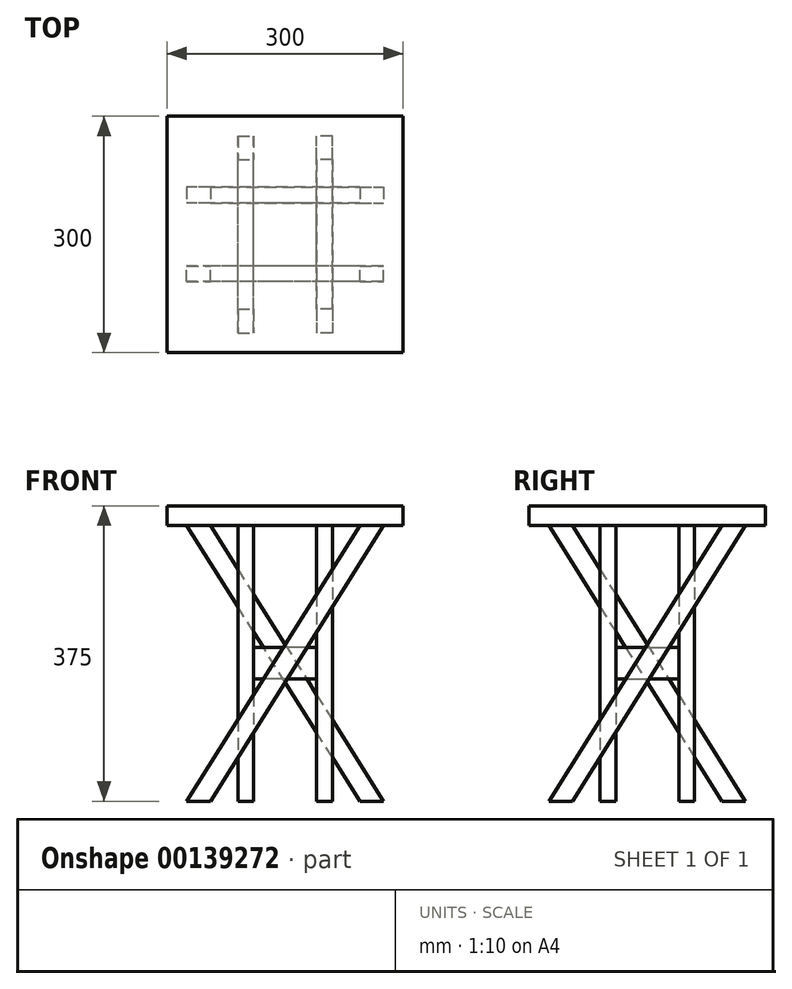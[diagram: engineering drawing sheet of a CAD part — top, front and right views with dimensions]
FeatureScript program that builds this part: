
annotation { "Feature Type Name" : "Feature", "Feature Type Description" : "" }
export const myFeature = defineFeature(function(context is Context, id is Id, definition is map)
    precondition{}
    {
        {
            var Q0;
            Q0=qCreatedBy(makeId("Top.planeOp"),FACE);
            var sketch = newSketch(context, id + "F0", { "sketchPlane" : qUnion([Q0])});
            skLineSegment(sketch, "E0.bottom", {"start": v(150, -150) * mm, "end": v(-150, -150) * mm});
            skLineSegment(sketch, "E0.top", {"start": v(150, 150) * mm, "end": v(-150, 150) * mm});
            skLineSegment(sketch, "E0.left", {"start": v(150, -150) * mm, "end": v(150, 150) * mm});
            skLineSegment(sketch, "E0.right", {"start": v(-150, -150) * mm, "end": v(-150, 150) * mm});
            skPoint(sketch, "E0.middle", {"position": v(0, 0) * mm});
            skLineSegment(sketch, "E1.bottom", {"start": v(40, -40) * mm, "end": v(-40, -40) * mm});
            skLineSegment(sketch, "E1.top", {"start": v(40, 40) * mm, "end": v(-40, 40) * mm});
            skLineSegment(sketch, "E1.left", {"start": v(40, -40) * mm, "end": v(40, 40) * mm});
            skLineSegment(sketch, "E1.right", {"start": v(-40, -40) * mm, "end": v(-40, 40) * mm});
            skSolve(sketch);
        }
        {
            var Q0;
            Q0=qCreatedBy(makeId("Front.planeOp"),FACE);
            var sketch = newSketch(context, id + "F1", { "sketchPlane" : qUnion([Q0])});
            skLineSegment(sketch, "E2.bottom", {"start": v(-125, 0) * mm, "end": v(125, 0) * mm, "construction": true});
            skLineSegment(sketch, "E2.top", {"start": v(-125, -350) * mm, "end": v(125, -350) * mm, "construction": true});
            skLineSegment(sketch, "E2.left", {"start": v(-125, 0) * mm, "end": v(-125, -350) * mm, "construction": true});
            skLineSegment(sketch, "E2.right", {"start": v(125, 0) * mm, "end": v(125, -350) * mm, "construction": true});
            skLineSegment(sketch, "E3", {"start": v(0, 0) * mm, "end": v(0, -350) * mm, "construction": true});
            skLineSegment(sketch, "E4", {"start": v(125, 0) * mm, "end": v(-125, -350) * mm, "construction": true});
            skLineSegment(sketch, "E5", {"start": v(-125, 0) * mm, "end": v(125, -350) * mm, "construction": true});
            skLineSegment(sketch, "E6", {"start": v(-95, 0) * mm, "end": v(125, -350) * mm});
            skLineSegment(sketch, "E7", {"start": v(95, -350) * mm, "end": v(-125, 0) * mm});
            skLineSegment(sketch, "E8", {"start": v(95, 0) * mm, "end": v(-125, -350) * mm});
            skLineSegment(sketch, "E9", {"start": v(125, 0) * mm, "end": v(-95, -350) * mm});
            skLineSegment(sketch, "E10", {"start": v(-125, -350) * mm, "end": v(-95, -350) * mm});
            skLineSegment(sketch, "E11", {"start": v(95, -350) * mm, "end": v(125, -350) * mm});
            skLineSegment(sketch, "E12", {"start": v(95, 0) * mm, "end": v(125, 0) * mm});
            skLineSegment(sketch, "E13", {"start": v(-95, 0) * mm, "end": v(-125, 0) * mm});
            skLineSegment(sketch, "E14", {"start": v(0, -175) * mm, "end": v(36.92, -175) * mm, "construction": true});
            skPoint(sketch, "E14.endSnap0", {"position": v(0, -175) * mm});
            skSolve(sketch);
        }
        {
            var Q0;
            Q0=makeQuery(id+"F0.imprint","IMPRINT",FACE,{"disambiguationData":[TD([[makeQuery(id+"F0.imprint","IMPRINT",EDGE,{"derivedFrom":sQuery(id+"F0.wireOp",EDGE,"E0.bottom")}),-1.0]])]});
            var Q1;
            Q1=sQuery(id+"F1.wireOp",EDGE,"E14");
            cPlane(context, id + "F2", {"entities" : qUnion([Q0, Q1]), "cplaneType" : CPlaneType.LINE_ANGLE, "offset" : 25 * mm, "angle" : 0 * degree, "width" : 150 * mm, "height" : 150 * mm});
        }
        {
            var Q0;
            Q0=qCreatedBy(id+"F2.planeOp",FACE);
            var sketch = newSketch(context, id + "F3", { "sketchPlane" : qUnion([Q0])});
            skLineSegment(sketch, "E15.0", {"start": v(-40, 40) * mm, "end": v(-40, -40) * mm});
            skLineSegment(sketch, "E15.1", {"start": v(40, -40) * mm, "end": v(-40, -40) * mm});
            skLineSegment(sketch, "E15.2", {"start": v(40, 40) * mm, "end": v(-40, 40) * mm});
            skLineSegment(sketch, "E15.3", {"start": v(40, 40) * mm, "end": v(40, -40) * mm});
            skSolve(sketch);
        }
        {
            var Q0;
            Q0=qCreatedBy(makeId("Front.planeOp"),FACE);
            var Q1;
            Q1=sQuery(id+"F3.wireOp",EDGE,"E15.1");
            cPlane(context, id + "F4", {"entities" : qUnion([Q0, Q1]), "cplaneType" : CPlaneType.LINE_ANGLE, "offset" : 25 * mm, "angle" : 0 * degree, "width" : 150 * mm, "height" : 150 * mm});
        }
        {
            var Q0;
            Q0=qCreatedBy(makeId("Front.planeOp"),FACE);
            var Q1;
            Q1=sQuery(id+"F3.wireOp",EDGE,"E15.2");
            cPlane(context, id + "F5", {"entities" : qUnion([Q0, Q1]), "cplaneType" : CPlaneType.LINE_ANGLE, "offset" : 25 * mm, "angle" : 0 * degree, "width" : 150 * mm, "height" : 150 * mm});
        }
        {
            var Q0;
            Q0=qCreatedBy(id+"F4.planeOp",FACE);
            var sketch = newSketch(context, id + "F6", { "sketchPlane" : qUnion([Q0])});
            skLineSegment(sketch, "E16.0", {"start": v(-95, -350) * mm, "end": v(125, 0) * mm});
            skLineSegment(sketch, "E16.1", {"start": v(95, 0) * mm, "end": v(-125, -350) * mm});
            skLineSegment(sketch, "E16.2", {"start": v(95, 0) * mm, "end": v(125, 0) * mm});
            skLineSegment(sketch, "E16.3", {"start": v(-95, -350) * mm, "end": v(-125, -350) * mm});
            skSolve(sketch);
        }
        {
            var Q0;
            Q0=qCreatedBy(id+"F5.planeOp",FACE);
            var sketch = newSketch(context, id + "F7", { "sketchPlane" : qUnion([Q0])});
            skLineSegment(sketch, "E17.0", {"start": v(-95, 0) * mm, "end": v(-125, 0) * mm});
            skLineSegment(sketch, "E17.1", {"start": v(-125, 0) * mm, "end": v(95, -350) * mm});
            skLineSegment(sketch, "E17.2", {"start": v(-95, 0) * mm, "end": v(125, -350) * mm});
            skLineSegment(sketch, "E17.3", {"start": v(125, -350) * mm, "end": v(95, -350) * mm});
            skSolve(sketch);
        }
        {
            var Q0;
            Q0=makeQuery(id+"F7.imprint","IMPRINT",FACE,{"disambiguationData":[TD([[makeQuery(id+"F7.imprint","IMPRINT",EDGE,{"derivedFrom":sQuery(id+"F7.wireOp",EDGE,"E17.0")}),1.0]])]});
            extrude(context, id + "F8", {"entities" : qUnion([Q0]), "oppositeDirection" : true, "depth" : 20 * mm});
        }
        {
            var Q0;
            Q0=makeQuery(id+"F6.imprint","IMPRINT",FACE,{"disambiguationData":[TD([[makeQuery(id+"F6.imprint","IMPRINT",EDGE,{"derivedFrom":sQuery(id+"F6.wireOp",EDGE,"E16.0")}),1.0]])]});
            extrude(context, id + "F9", {"entities" : qUnion([Q0]), "depth" : 20 * mm});
        }
        {
            var Q0;
            Q0=makeQuery(id+"F8.opExtrude","SWEPT_BODY",BODY,{"disambiguationData":[OSD([sQuery(id+"F7.wireOp",EDGE,"E17.0"),sQuery(id+"F7.wireOp",EDGE,"E17.1"),sQuery(id+"F7.wireOp",EDGE,"E17.2"),sQuery(id+"F7.wireOp",EDGE,"E17.3")])]});
            var Q1;
            Q1=makeQuery(id+"F9.opExtrude","SWEPT_BODY",BODY,{"disambiguationData":[OSD([sQuery(id+"F6.wireOp",EDGE,"E16.0"),sQuery(id+"F6.wireOp",EDGE,"E16.1"),sQuery(id+"F6.wireOp",EDGE,"E16.2"),sQuery(id+"F6.wireOp",EDGE,"E16.3")])]});
            var Q2;
            Q2=sQuery(id+"F1.wireOp",EDGE,"E3");
            circularPattern(context, id + "F10", {"entities" : qUnion([Q0, Q1]), "axis" : qUnion([Q2]), "angle" : 90 * degree, "instanceCount" : 2});
        }
        {
            var Q0;
            Q0=makeQuery(id+"F3.imprint","IMPRINT",FACE,{"disambiguationData":[TD([[makeQuery(id+"F3.imprint","IMPRINT",EDGE,{"derivedFrom":sQuery(id+"F3.wireOp",EDGE,"E15.0")}),1.0]])]});
            extrude(context, id + "F11", {"entities" : qUnion([Q0]), "endBound" : BoundingType.SYMMETRIC, "depth" : 40 * mm});
        }
        {
            var Q0;
            Q0=makeQuery(id+"F0.imprint","IMPRINT",FACE,{"disambiguationData":[TD([[makeQuery(id+"F0.imprint","IMPRINT",EDGE,{"derivedFrom":sQuery(id+"F0.wireOp",EDGE,"E0.bottom")}),-1.0]])]});
            var Q1;
            Q1=makeQuery(id+"F0.imprint","IMPRINT",FACE,{"disambiguationData":[TD([[makeQuery(id+"F0.imprint","IMPRINT",EDGE,{"derivedFrom":sQuery(id+"F0.wireOp",EDGE,"E1.bottom")}),-1.0]])]});
            extrude(context, id + "F12", {"entities" : qUnion([Q0, Q1]), "depth" : 25 * mm});
        }
    });
